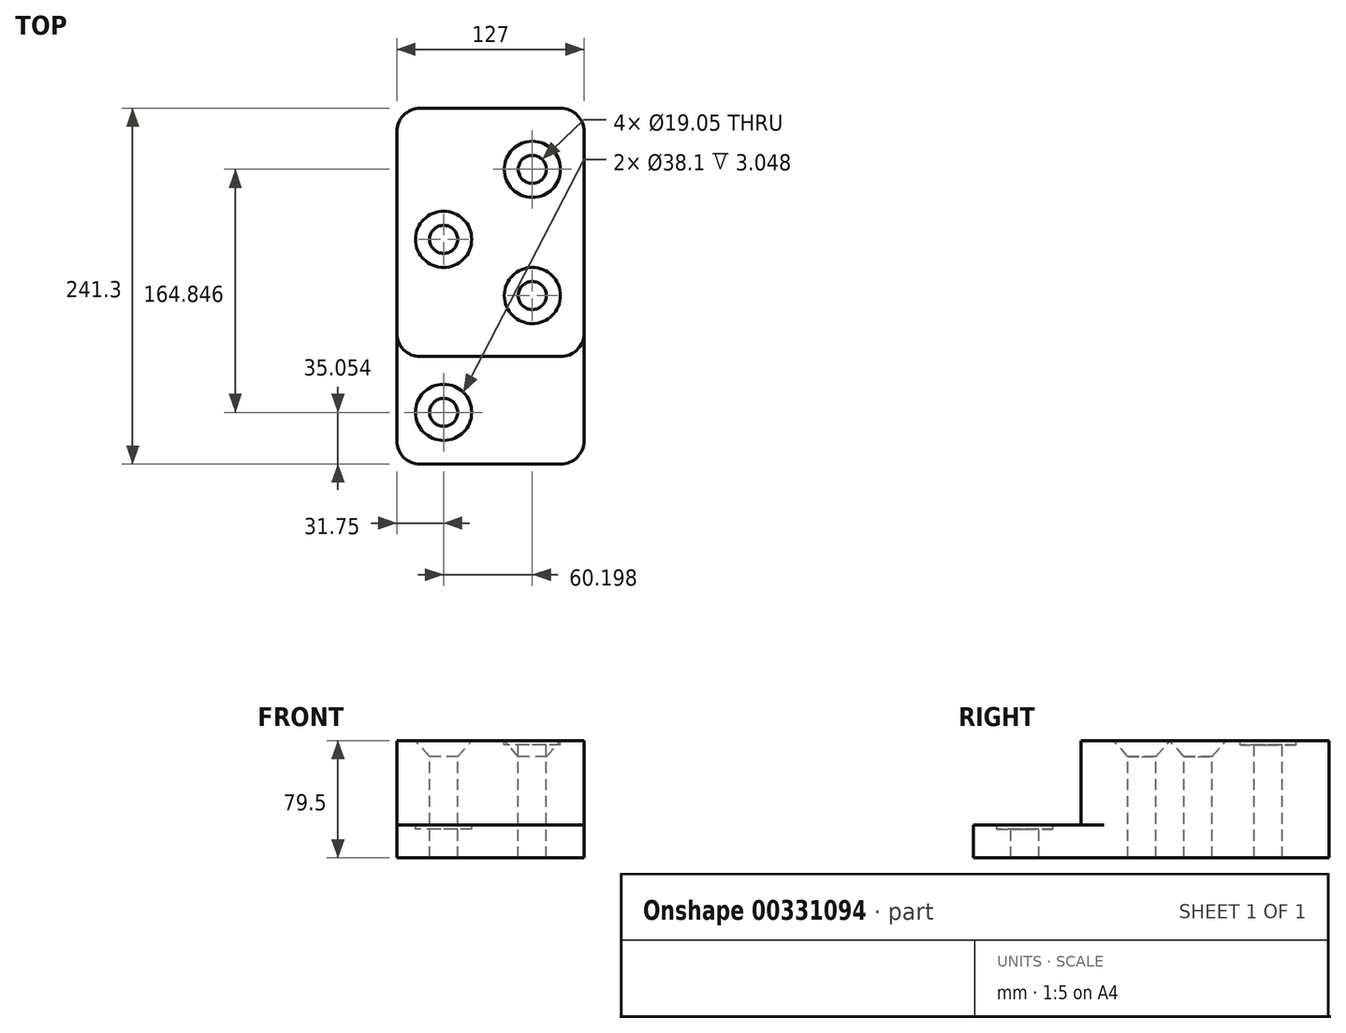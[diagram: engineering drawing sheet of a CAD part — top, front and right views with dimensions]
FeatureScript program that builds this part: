
annotation { "Feature Type Name" : "Feature", "Feature Type Description" : "" }
export const myFeature = defineFeature(function(context is Context, id is Id, definition is map)
    precondition{}
    {
        {
            var Q0;
            Q0=qCreatedBy(makeId("Top.planeOp"),FACE);
            var sketch = newSketch(context, id + "F0", { "sketchPlane" : qUnion([Q0])});
            skLineSegment(sketch, "E0", {"start": v(-47.75, 168.4) * mm, "end": v(47.75, 168.4) * mm});
            skLineSegment(sketch, "E1", {"start": v(63.5, 152.65) * mm, "end": v(63.5, 15.75) * mm});
            skLineSegment(sketch, "E2", {"start": v(-63.5, 152.65) * mm, "end": v(-63.5, 15.75) * mm});
            skLineSegment(sketch, "E3", {"start": v(-47.75, 0) * mm, "end": v(47.75, 0) * mm});
            skLineSegment(sketch, "E4", {"start": v(-47.75, -72.9) * mm, "end": v(47.75, -72.9) * mm});
            skLineSegment(sketch, "E5", {"start": v(63.5, -57.15) * mm, "end": v(63.5, 15.75) * mm});
            skLineSegment(sketch, "E6", {"start": v(-63.5, -57.15) * mm, "end": v(-63.5, 15.75) * mm});
            skArc(sketch, "E7", {"start": v(-47.75, 0) * mm, "mid": v(-58.89, 4.61) * mm, "end": v(-63.5, 15.75) * mm});
            skArc(sketch, "E8", {"start": v(-47.75, 168.4) * mm, "mid": v(-58.89, 163.79) * mm, "end": v(-63.5, 152.65) * mm});
            skArc(sketch, "E9", {"start": v(63.5, 152.65) * mm, "mid": v(58.89, 163.79) * mm, "end": v(47.75, 168.4) * mm});
            skArc(sketch, "E10", {"start": v(63.5, 15.75) * mm, "mid": v(58.89, 4.61) * mm, "end": v(47.75, 0) * mm});
            skArc(sketch, "E11", {"start": v(63.5, -57.15) * mm, "mid": v(58.89, -68.29) * mm, "end": v(47.75, -72.9) * mm});
            skArc(sketch, "E12", {"start": v(-47.75, -72.9) * mm, "mid": v(-58.89, -68.29) * mm, "end": v(-63.5, -57.15) * mm});
            skPoint(sketch, "E13", {"position": v(-31.75, 79.5) * mm});
            skPoint(sketch, "E14", {"position": v(28.45, 127) * mm});
            skPoint(sketch, "E15", {"position": v(28.45, 41.4) * mm});
            skPoint(sketch, "E16", {"position": v(-31.75, -37.85) * mm});
            skSolve(sketch);
        }
        {
            var Q0;
            Q0=makeQuery(id+"F0.imprint","IMPRINT",FACE,{"disambiguationData":[TD([[makeQuery(id+"F0.imprint","IMPRINT",EDGE,{"derivedFrom":sQuery(id+"F0.wireOp",EDGE,"E0")}),-1.0]])]});
            extrude(context, id + "F1", {"entities" : qUnion([Q0]), "depth" : 79.5 * mm});
        }
        {
            var Q0;
            Q0=makeQuery(id+"F0.imprint","IMPRINT",FACE,{"disambiguationData":[TD([[makeQuery(id+"F0.imprint","IMPRINT",EDGE,{"derivedFrom":sQuery(id+"F0.wireOp",EDGE,"E3")}),-1.0]])]});
            extrude(context, id + "F2", {"entities" : qUnion([Q0]), "operationType" : NewBodyOperationType.ADD, "depth" : 22.35 * mm});
        }
        {
            var Q0;
            Q0=makeQuery(id+"F1.opExtrude","CAP_FACE",FACE,{"disambiguationData":[OSD([sQuery(id+"F0.wireOp",EDGE,"E0"),sQuery(id+"F0.wireOp",EDGE,"E1"),sQuery(id+"F0.wireOp",EDGE,"E2"),sQuery(id+"F0.wireOp",EDGE,"E3"),sQuery(id+"F0.wireOp",EDGE,"E7"),sQuery(id+"F0.wireOp",EDGE,"E8"),sQuery(id+"F0.wireOp",EDGE,"E9"),sQuery(id+"F0.wireOp",EDGE,"E10")])],"isStart":false});
            var sketch = newSketch(context, id + "F3", { "sketchPlane" : qUnion([Q0])});
            skPoint(sketch, "E17.0", {"position": v(28.45, 41.4) * mm});
            skPoint(sketch, "E17.1", {"position": v(-31.75, 79.5) * mm});
            skPoint(sketch, "E17.2", {"position": v(28.45, 127) * mm});
            skSolve(sketch);
        }
        {
            var Q0;
            Q0=sQuery(id+"F3.wireOp",VERTEX,"E17.1");
            var Q1;
            Q1=sQuery(id+"F3.wireOp",VERTEX,"E17.0");
            var Q2;
            Q2=makeQuery(id+"F1.opExtrude","SWEPT_BODY",BODY,{"disambiguationData":[OSD([sQuery(id+"F0.wireOp",EDGE,"E0"),sQuery(id+"F0.wireOp",EDGE,"E1"),sQuery(id+"F0.wireOp",EDGE,"E2"),sQuery(id+"F0.wireOp",EDGE,"E3"),sQuery(id+"F0.wireOp",EDGE,"E7"),sQuery(id+"F0.wireOp",EDGE,"E8"),sQuery(id+"F0.wireOp",EDGE,"E9"),sQuery(id+"F0.wireOp",EDGE,"E10")])]});
            hole(context, id + "F4", {"style" : HoleStyle.C_SINK, "endStyle" : HoleEndStyle.THROUGH, "holeDiameter" : 19.05 * mm, "cSinkDiameter" : 38.1 * mm, "cSinkAngle" : 82 * degree, "tappedDepth" : 12.7 * mm, "tapClearance" : 3, "locations" : qUnion([Q0, Q1]), "scope" : qUnion([Q2])});
        }
        {
            var Q0;
            Q0=makeQuery(id+"F2.opExtrude","CAP_FACE",FACE,{"disambiguationData":[OSD([sQuery(id+"F0.wireOp",EDGE,"E3"),sQuery(id+"F0.wireOp",EDGE,"E4"),sQuery(id+"F0.wireOp",EDGE,"E5"),sQuery(id+"F0.wireOp",EDGE,"E6"),sQuery(id+"F0.wireOp",EDGE,"E7"),sQuery(id+"F0.wireOp",EDGE,"E10"),sQuery(id+"F0.wireOp",EDGE,"E11"),sQuery(id+"F0.wireOp",EDGE,"E12")])],"isStart":false});
            var sketch = newSketch(context, id + "F5", { "sketchPlane" : qUnion([Q0])});
            skPoint(sketch, "E18.0", {"position": v(-31.75, -37.85) * mm});
            skSolve(sketch);
        }
        {
            var Q0;
            Q0=sQuery(id+"F5.wireOp",VERTEX,"E18.0");
            var Q1;
            Q1=sQuery(id+"F3.wireOp",VERTEX,"E17.2");
            var Q2;
            Q2=makeQuery(id+"F1.opExtrude","SWEPT_BODY",BODY,{"disambiguationData":[OSD([sQuery(id+"F0.wireOp",EDGE,"E0"),sQuery(id+"F0.wireOp",EDGE,"E1"),sQuery(id+"F0.wireOp",EDGE,"E2"),sQuery(id+"F0.wireOp",EDGE,"E3"),sQuery(id+"F0.wireOp",EDGE,"E7"),sQuery(id+"F0.wireOp",EDGE,"E8"),sQuery(id+"F0.wireOp",EDGE,"E9"),sQuery(id+"F0.wireOp",EDGE,"E10")])]});
            hole(context, id + "F6", {"style" : HoleStyle.C_BORE, "endStyle" : HoleEndStyle.THROUGH, "holeDiameter" : 19.05 * mm, "cBoreDiameter" : 38.1 * mm, "cBoreDepth" : 3.05 * mm, "tappedDepth" : 12.7 * mm, "tapClearance" : 3, "locations" : qUnion([Q0, Q1]), "scope" : qUnion([Q2])});
        }
    });
